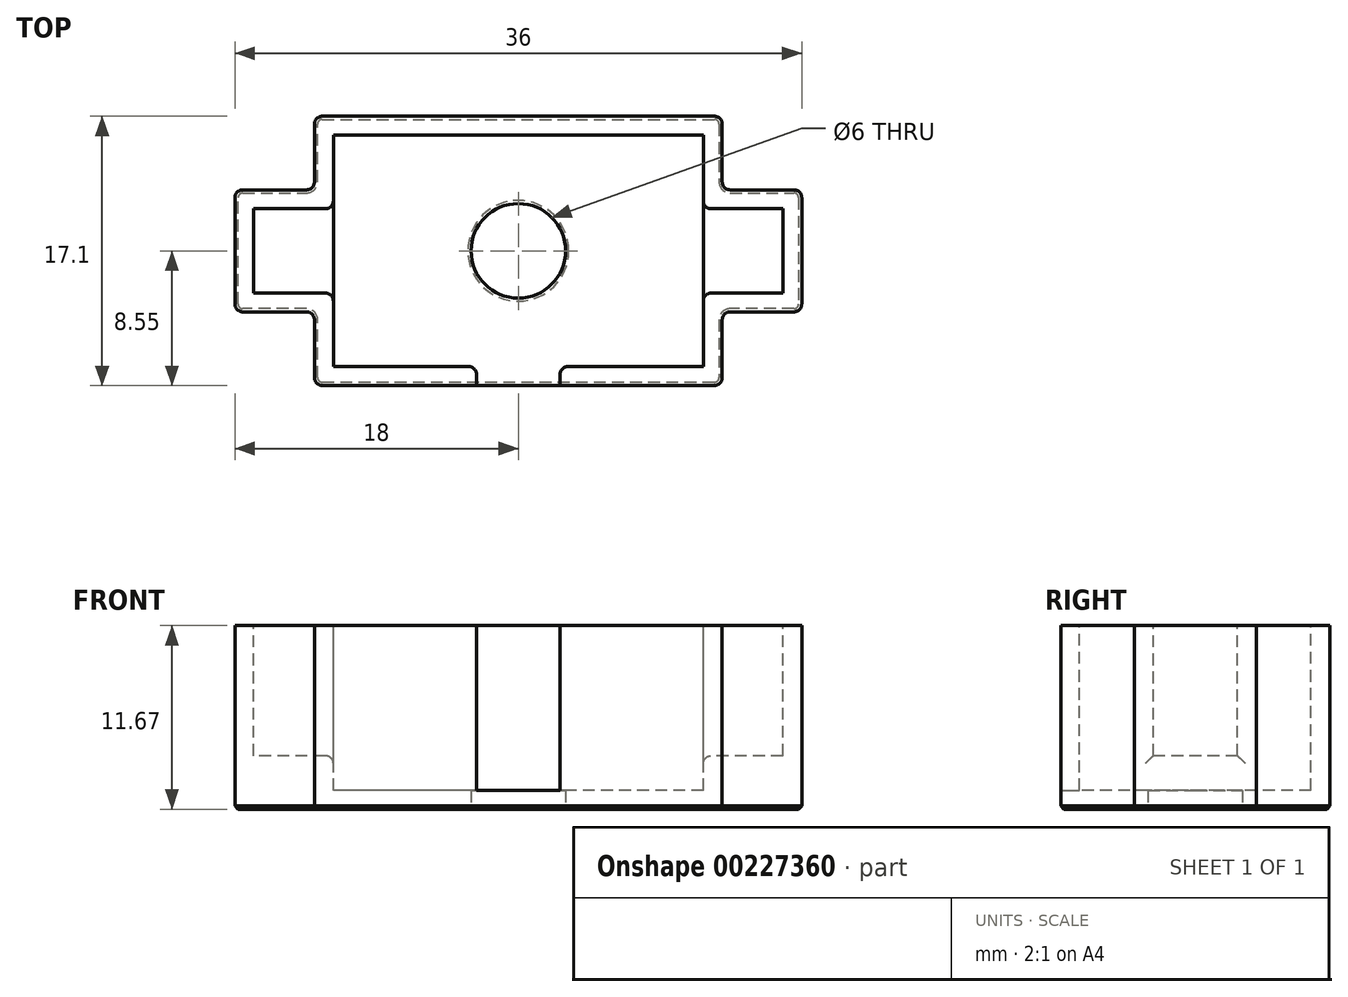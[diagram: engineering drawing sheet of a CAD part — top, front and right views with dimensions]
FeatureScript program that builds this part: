
annotation { "Feature Type Name" : "Feature", "Feature Type Description" : "" }
export const myFeature = defineFeature(function(context is Context, id is Id, definition is map)
    precondition{}
    {
        {
            var Q0;
            Q0=qCreatedBy(makeId("Top.planeOp"),FACE);
            var sketch = newSketch(context, id + "F0", { "sketchPlane" : qUnion([Q0])});
            skLineSegment(sketch, "E0.bottom", {"start": v(11.6, 7.2) * mm, "end": v(-11.6, 7.2) * mm, "construction": true});
            skLineSegment(sketch, "E0.top", {"start": v(11.6, -7.2) * mm, "end": v(2.5, -7.2) * mm, "construction": true});
            skLineSegment(sketch, "E0.left", {"start": v(11.6, 7.2) * mm, "end": v(11.6, 2.52) * mm, "construction": true});
            skLineSegment(sketch, "E0.right", {"start": v(-11.6, 7.2) * mm, "end": v(-11.6, 2.52) * mm, "construction": true});
            skPoint(sketch, "E0.middle", {"position": v(0, 0) * mm});
            skLineSegment(sketch, "E1.bottom", {"start": v(16.65, 2.52) * mm, "end": v(11.6, 2.52) * mm, "construction": true});
            skLineSegment(sketch, "E1.top", {"start": v(16.65, -2.52) * mm, "end": v(11.6, -2.52) * mm, "construction": true});
            skLineSegment(sketch, "E1.left", {"start": v(16.65, 2.52) * mm, "end": v(16.65, -2.52) * mm, "construction": true});
            skLineSegment(sketch, "E1.right", {"start": v(-16.65, 2.52) * mm, "end": v(-16.65, -2.52) * mm, "construction": true});
            skCircle(sketch, "E2", {"center": v(-14, 0) * mm, "radius": 1.5 * mm, "construction": true});
            skCircle(sketch, "E3.MirrorC", {"center": v(14, 0) * mm, "radius": 1.5 * mm, "construction": true});
            skLineSegment(sketch, "E4", {"start": v(-2.5, -7.2) * mm, "end": v(-2.5, -16.1) * mm, "construction": true});
            skLineSegment(sketch, "E5", {"start": v(-2.5, -16.1) * mm, "end": v(2.5, -16.1) * mm, "construction": true});
            skLineSegment(sketch, "E6", {"start": v(2.5, -16.1) * mm, "end": v(2.5, -7.2) * mm, "construction": true});
            skLineSegment(sketch, "E7", {"start": v(-2.5, -7.2) * mm, "end": v(-11.6, -7.2) * mm, "construction": true});
            skLineSegment(sketch, "E8", {"start": v(2.5, -7.2) * mm, "end": v(-2.5, -7.2) * mm, "construction": true});
            skLineSegment(sketch, "E9", {"start": v(-11.6, 2.52) * mm, "end": v(-16.65, 2.52) * mm, "construction": true});
            skLineSegment(sketch, "E10", {"start": v(-11.6, -2.52) * mm, "end": v(-16.65, -2.52) * mm, "construction": true});
            skLineSegment(sketch, "E11", {"start": v(11.6, -2.52) * mm, "end": v(-11.6, -2.52) * mm, "construction": true});
            skLineSegment(sketch, "E12", {"start": v(11.6, 2.52) * mm, "end": v(-11.6, 2.52) * mm, "construction": true});
            skLineSegment(sketch, "E13", {"start": v(-11.6, 2.52) * mm, "end": v(-11.6, -2.52) * mm, "construction": true});
            skLineSegment(sketch, "E14", {"start": v(-11.6, -2.52) * mm, "end": v(-11.6, -7.2) * mm, "construction": true});
            skLineSegment(sketch, "E15", {"start": v(11.6, -2.52) * mm, "end": v(11.6, -7.2) * mm, "construction": true});
            skLineSegment(sketch, "E16", {"start": v(11.6, 2.52) * mm, "end": v(11.6, -2.52) * mm, "construction": true});
            skSolve(sketch);
        }
        {
            var Q0;
            Q0=qCreatedBy(makeId("Front.planeOp"),FACE);
            var sketch = newSketch(context, id + "F1", { "sketchPlane" : qUnion([Q0])});
            skLineSegment(sketch, "E17", {"start": v(0, 1.2) * mm, "end": v(0, 0) * mm});
            skLineSegment(sketch, "E18", {"start": v(0, 1.2) * mm, "end": v(0, 3.4) * mm});
            skLineSegment(sketch, "E19", {"start": v(0, 3.4) * mm, "end": v(0, 4.67) * mm});
            skLineSegment(sketch, "E20", {"start": v(0, 4.67) * mm, "end": v(0, 11.67) * mm});
            skSolve(sketch);
        }
        {
            var Q0;
            Q0=sQuery(id+"F1.wireOp",VERTEX,"E17.start");
            var Q1;
            Q1=sQuery(id+"F1.wireOp",EDGE,"E18");
            cPlane(context, id + "F2", {"entities" : qUnion([Q0, Q1]), "cplaneType" : CPlaneType.LINE_POINT, "offset" : 25 * mm, "width" : 150 * mm, "height" : 150 * mm});
        }
        {
            var Q0;
            Q0=qCreatedBy(makeId("Top.planeOp"),FACE);
            var sketch = newSketch(context, id + "F3", { "sketchPlane" : qUnion([Q0])});
            skLineSegment(sketch, "E21.0", {"start": v(-16.65, 2.52) * mm, "end": v(-16.65, -2.52) * mm, "construction": true});
            skLineSegment(sketch, "E22.0", {"start": v(16.65, 2.52) * mm, "end": v(16.65, -2.52) * mm, "construction": true});
            skLineSegment(sketch, "E23.bottom", {"start": v(17.85, 8.4) * mm, "end": v(-17.85, 8.4) * mm});
            skLineSegment(sketch, "E23.top", {"start": v(17.85, -8.4) * mm, "end": v(-17.85, -8.4) * mm});
            skLineSegment(sketch, "E23.left", {"start": v(17.85, 8.4) * mm, "end": v(17.85, -8.4) * mm});
            skLineSegment(sketch, "E23.right", {"start": v(-17.85, 8.4) * mm, "end": v(-17.85, -8.4) * mm});
            skPoint(sketch, "E23.middle", {"position": v(0, 0) * mm});
            skLineSegment(sketch, "E24.0", {"start": v(11.6, 7.2) * mm, "end": v(-11.6, 7.2) * mm, "construction": true});
            skLineSegment(sketch, "E25.0", {"start": v(-2.5, -7.2) * mm, "end": v(-11.6, -7.2) * mm, "construction": true});
            skLineSegment(sketch, "E26.0", {"start": v(11.6, -7.2) * mm, "end": v(2.5, -7.2) * mm, "construction": true});
            skSolve(sketch);
        }
        {
            var Q0;
            Q0=qCreatedBy(id+"F2.planeOp",FACE);
            var sketch = newSketch(context, id + "F4", { "sketchPlane" : qUnion([Q0])});
            skLineSegment(sketch, "E27.0", {"start": v(11.75, 7.35) * mm, "end": v(11.75, 2.67) * mm});
            skLineSegment(sketch, "E27.1", {"start": v(16.8, 2.67) * mm, "end": v(11.75, 2.67) * mm});
            skLineSegment(sketch, "E27.2", {"start": v(16.8, 2.68) * mm, "end": v(16.8, -2.68) * mm});
            skLineSegment(sketch, "E27.3", {"start": v(16.8, -2.67) * mm, "end": v(11.75, -2.67) * mm});
            skLineSegment(sketch, "E27.4", {"start": v(11.75, -2.67) * mm, "end": v(11.75, -7.35) * mm});
            skLineSegment(sketch, "E27.5", {"start": v(-11.75, -2.67) * mm, "end": v(-16.8, -2.67) * mm});
            skLineSegment(sketch, "E27.6", {"start": v(-16.8, 2.67) * mm, "end": v(-16.8, -2.68) * mm});
            skLineSegment(sketch, "E27.7", {"start": v(-11.75, 2.67) * mm, "end": v(-16.8, 2.67) * mm});
            skLineSegment(sketch, "E27.8", {"start": v(-11.75, 7.35) * mm, "end": v(-11.75, 2.67) * mm});
            skLineSegment(sketch, "E27.9", {"start": v(-11.75, -2.68) * mm, "end": v(-11.75, -7.35) * mm});
            skLineSegment(sketch, "E27.10", {"start": v(-2.65, -7.35) * mm, "end": v(-11.75, -7.35) * mm});
            skLineSegment(sketch, "E27.11", {"start": v(-2.65, -7.35) * mm, "end": v(-2.65, -16.26) * mm});
            skLineSegment(sketch, "E27.12", {"start": v(-2.65, -16.26) * mm, "end": v(2.65, -16.26) * mm});
            skLineSegment(sketch, "E27.13", {"start": v(2.65, -16.26) * mm, "end": v(2.65, -7.35) * mm});
            skLineSegment(sketch, "E27.14", {"start": v(11.75, 7.35) * mm, "end": v(-11.75, 7.35) * mm});
            skLineSegment(sketch, "E27.15", {"start": v(11.75, -7.35) * mm, "end": v(2.65, -7.35) * mm});
            skLineSegment(sketch, "E28", {"start": v(-11.75, 2.67) * mm, "end": v(-11.75, -2.67) * mm});
            skLineSegment(sketch, "E29", {"start": v(11.75, 2.67) * mm, "end": v(11.75, -2.67) * mm});
            skSolve(sketch);
        }
        {
            var Q0;
            Q0=qCreatedBy(makeId("Top.planeOp"),FACE);
            var sketch = newSketch(context, id + "F5", { "sketchPlane" : qUnion([Q0])});
            skLineSegment(sketch, "E30.0", {"start": v(0, -8.55) * mm, "end": v(-12.95, -8.55) * mm});
            skLineSegment(sketch, "E30.1", {"start": v(-12.95, -3.87) * mm, "end": v(-12.95, -8.55) * mm});
            skLineSegment(sketch, "E30.2", {"start": v(-12.95, -3.87) * mm, "end": v(-18, -3.87) * mm});
            skLineSegment(sketch, "E30.3", {"start": v(18, 3.87) * mm, "end": v(18, -3.88) * mm});
            skLineSegment(sketch, "E30.4", {"start": v(18, -3.87) * mm, "end": v(12.95, -3.87) * mm});
            skLineSegment(sketch, "E30.5", {"start": v(12.95, -3.87) * mm, "end": v(12.95, -8.55) * mm});
            skLineSegment(sketch, "E30.6", {"start": v(12.95, -8.55) * mm, "end": v(0, -8.55) * mm});
            skLineSegment(sketch, "E30.7", {"start": v(18, 3.87) * mm, "end": v(12.95, 3.87) * mm});
            skLineSegment(sketch, "E30.8", {"start": v(12.95, 8.55) * mm, "end": v(12.95, 3.87) * mm});
            skLineSegment(sketch, "E30.9", {"start": v(12.95, 8.55) * mm, "end": v(-12.95, 8.55) * mm});
            skLineSegment(sketch, "E30.10", {"start": v(-12.95, 8.55) * mm, "end": v(-12.95, 3.87) * mm});
            skLineSegment(sketch, "E30.11", {"start": v(-12.95, 3.87) * mm, "end": v(-18, 3.87) * mm});
            skLineSegment(sketch, "E30.12", {"start": v(-18, 3.87) * mm, "end": v(-18, -3.87) * mm});
            skSolve(sketch);
        }
        {
            var Q0;
            Q0 = qSketchRegion(id + "F5", true);
            var Q1;
            Q1=sQuery(id+"F1.wireOp",EDGE,"E17");
            var Q2;
            Q2=sQuery(id+"F1.wireOp",EDGE,"E18");
            var Q3;
            Q3=sQuery(id+"F1.wireOp",EDGE,"E19");
            var Q4;
            Q4=sQuery(id+"F1.wireOp",EDGE,"E20");
            sweep(context, id + "F6", {"profiles" : qUnion([Q0]), "path" : qUnion([Q1, Q2, Q3, Q4])});
        }
        {
            var Q0;
            Q0 = qSketchRegion(id + "F4", true);
            var Q1;
            Q1=sQuery(id+"F1.wireOp",EDGE,"E18");
            var Q2;
            Q2=sQuery(id+"F1.wireOp",EDGE,"E19");
            var Q3;
            Q3=sQuery(id+"F1.wireOp",EDGE,"E20");
            sweep(context, id + "F7", {"operationType" : NewBodyOperationType.REMOVE, "profiles" : qUnion([Q0]), "path" : qUnion([Q1, Q2, Q3])});
        }
        {
            var Q0;
            Q0=makeQuery(id+"F4.imprint","IMPRINT",FACE,{"disambiguationData":[TD([[makeQuery(id+"F4.imprint","IMPRINT",EDGE,{"derivedFrom":sQuery(id+"F4.wireOp",EDGE,"E27.5")}),-1.0]])]});
            var Q1;
            Q1=makeQuery(id+"F4.imprint","IMPRINT",FACE,{"disambiguationData":[TD([[makeQuery(id+"F4.imprint","IMPRINT",EDGE,{"derivedFrom":sQuery(id+"F4.wireOp",EDGE,"E27.1")}),1.0]])]});
            var Q2;
            Q2=sQuery(id+"F1.wireOp",EDGE,"E18");
            sweep(context, id + "F8", {"operationType" : NewBodyOperationType.ADD, "profiles" : qUnion([Q0, Q1]), "path" : qUnion([Q2])});
        }
        {
            var Q0;
            Q0=qCreatedBy(makeId("Top.planeOp"),FACE);
            var sketch = newSketch(context, id + "F9", { "sketchPlane" : qUnion([Q0])});
            skCircle(sketch, "E31", {"center": v(0, 0) * mm, "radius": 3 * mm});
            skSolve(sketch);
        }
        {
            var Q0;
            Q0 = qSketchRegion(id + "F9", true);
            extrude(context, id + "F10", {"entities" : qUnion([Q0]), "operationType" : NewBodyOperationType.REMOVE, "endBound" : BoundingType.THROUGH_ALL, "depth" : 25 * mm});
        }
        {
            var Q0;
            Q0=makeQuery(id+"F7.boolean.opBoolean","COPY",EDGE,{"derivedFrom":makeQuery(id+"F7.opSweep","SWEPT_EDGE",EDGE,{"disambiguationData":[OSD([sQuery(id+"F1.wireOp",EDGE,"E18"),sQuery(id+"F4.wireOp",EDGE,"E27.7"),sQuery(id+"F4.wireOp",EDGE,"E27.8"),sQuery(id+"F4.wireOp",EDGE,"E28")])]})});
            var Q1;
            Q1=makeQuery(id+"F7.boolean.opBoolean","COPY",EDGE,{"derivedFrom":makeQuery(id+"F7.opSweep","SWEPT_EDGE",EDGE,{"disambiguationData":[OSD([sQuery(id+"F1.wireOp",EDGE,"E18"),sQuery(id+"F4.wireOp",EDGE,"E27.5"),sQuery(id+"F4.wireOp",EDGE,"E27.9"),sQuery(id+"F4.wireOp",EDGE,"E28")])]})});
            var Q2;
            Q2=makeQuery(id+"F7.boolean.opBoolean","COPY",EDGE,{"derivedFrom":makeQuery(id+"F7.opSweep","SWEPT_EDGE",EDGE,{"disambiguationData":[OSD([sQuery(id+"F1.wireOp",EDGE,"E18"),sQuery(id+"F4.wireOp",EDGE,"E27.0"),sQuery(id+"F4.wireOp",EDGE,"E27.1"),sQuery(id+"F4.wireOp",EDGE,"E29")])]})});
            var Q3;
            Q3=makeQuery(id+"F7.boolean.opBoolean","COPY",EDGE,{"derivedFrom":makeQuery(id+"F7.opSweep","SWEPT_EDGE",EDGE,{"disambiguationData":[OSD([sQuery(id+"F1.wireOp",EDGE,"E18"),sQuery(id+"F4.wireOp",EDGE,"E27.3"),sQuery(id+"F4.wireOp",EDGE,"E27.4"),sQuery(id+"F4.wireOp",EDGE,"E29")])]})});
            var Q4;
            Q4=makeQuery(id+"F7.boolean.opBoolean","COPY",EDGE,{"derivedFrom":makeQuery(id+"F7.opSweep","SWEPT_EDGE",EDGE,{"disambiguationData":[OSD([sQuery(id+"F1.wireOp",EDGE,"E18"),sQuery(id+"F4.wireOp",EDGE,"E27.10"),sQuery(id+"F4.wireOp",EDGE,"E27.11")])]})});
            var Q5;
            Q5=makeQuery(id+"F7.boolean.opBoolean","COPY",EDGE,{"derivedFrom":makeQuery(id+"F7.opSweep","SWEPT_EDGE",EDGE,{"disambiguationData":[OSD([sQuery(id+"F1.wireOp",EDGE,"E18"),sQuery(id+"F4.wireOp",EDGE,"E27.13"),sQuery(id+"F4.wireOp",EDGE,"E27.15")])]})});
            var Q6;
            Q6=makeQuery(id+"F8.opSweep","CAP_EDGE",EDGE,{"disambiguationData":[OSD([sQuery(id+"F1.wireOp",VERTEX,"E18.end"),sQuery(id+"F4.wireOp",EDGE,"E28")])],"isStart":false});
            var Q7;
            Q7=makeQuery(id+"F8.opSweep","CAP_EDGE",EDGE,{"disambiguationData":[OSD([sQuery(id+"F1.wireOp",VERTEX,"E18.end"),sQuery(id+"F4.wireOp",EDGE,"E29")])],"isStart":false});
            var Q8;
            Q8=makeQuery(id+"F6.opSweep","SWEPT_EDGE",EDGE,{"disambiguationData":[OSD([sQuery(id+"F1.wireOp",EDGE,"E17"),sQuery(id+"F5.wireOp",EDGE,"E30.3"),sQuery(id+"F5.wireOp",EDGE,"E30.4")])]});
            var Q9;
            Q9=makeQuery(id+"F6.opSweep","SWEPT_EDGE",EDGE,{"disambiguationData":[OSD([sQuery(id+"F1.wireOp",EDGE,"E17"),sQuery(id+"F5.wireOp",EDGE,"E30.3"),sQuery(id+"F5.wireOp",EDGE,"E30.7")])]});
            var Q10;
            Q10=makeQuery(id+"F6.opSweep","SWEPT_EDGE",EDGE,{"disambiguationData":[OSD([sQuery(id+"F1.wireOp",EDGE,"E17"),sQuery(id+"F5.wireOp",EDGE,"E30.5"),sQuery(id+"F5.wireOp",EDGE,"E30.6")])]});
            var Q11;
            Q11=makeQuery(id+"F6.opSweep","SWEPT_EDGE",EDGE,{"disambiguationData":[OSD([sQuery(id+"F1.wireOp",EDGE,"E17"),sQuery(id+"F5.wireOp",EDGE,"E30.8"),sQuery(id+"F5.wireOp",EDGE,"E30.9")])]});
            var Q12;
            Q12=makeQuery(id+"F6.opSweep","SWEPT_EDGE",EDGE,{"disambiguationData":[OSD([sQuery(id+"F1.wireOp",EDGE,"E17"),sQuery(id+"F5.wireOp",EDGE,"E30.0"),sQuery(id+"F5.wireOp",EDGE,"E30.1")])]});
            var Q13;
            Q13=makeQuery(id+"F6.opSweep","SWEPT_EDGE",EDGE,{"disambiguationData":[OSD([sQuery(id+"F1.wireOp",EDGE,"E17"),sQuery(id+"F5.wireOp",EDGE,"E30.2"),sQuery(id+"F5.wireOp",EDGE,"E30.12")])]});
            var Q14;
            Q14=makeQuery(id+"F6.opSweep","SWEPT_EDGE",EDGE,{"disambiguationData":[OSD([sQuery(id+"F1.wireOp",EDGE,"E17"),sQuery(id+"F5.wireOp",EDGE,"E30.9"),sQuery(id+"F5.wireOp",EDGE,"E30.10")])]});
            var Q15;
            Q15=makeQuery(id+"F6.opSweep","SWEPT_EDGE",EDGE,{"disambiguationData":[OSD([sQuery(id+"F1.wireOp",EDGE,"E17"),sQuery(id+"F5.wireOp",EDGE,"E30.11"),sQuery(id+"F5.wireOp",EDGE,"E30.12")])]});
            var Q16;
            Q16=makeQuery(id+"F6.opSweep","SWEPT_EDGE",EDGE,{"disambiguationData":[OSD([sQuery(id+"F1.wireOp",EDGE,"E17"),sQuery(id+"F5.wireOp",EDGE,"E30.7"),sQuery(id+"F5.wireOp",EDGE,"E30.8")])]});
            var Q17;
            Q17=makeQuery(id+"F6.opSweep","SWEPT_EDGE",EDGE,{"disambiguationData":[OSD([sQuery(id+"F1.wireOp",EDGE,"E17"),sQuery(id+"F5.wireOp",EDGE,"E30.4"),sQuery(id+"F5.wireOp",EDGE,"E30.5")])]});
            var Q18;
            Q18=makeQuery(id+"F6.opSweep","SWEPT_EDGE",EDGE,{"disambiguationData":[OSD([sQuery(id+"F1.wireOp",EDGE,"E17"),sQuery(id+"F5.wireOp",EDGE,"E30.1"),sQuery(id+"F5.wireOp",EDGE,"E30.2")])]});
            var Q19;
            Q19=makeQuery(id+"F6.opSweep","SWEPT_EDGE",EDGE,{"disambiguationData":[OSD([sQuery(id+"F1.wireOp",EDGE,"E17"),sQuery(id+"F5.wireOp",EDGE,"E30.10"),sQuery(id+"F5.wireOp",EDGE,"E30.11")])]});
            fillet(context, id + "F11", {"entities" : qUnion([Q0, Q1, Q2, Q3, Q4, Q5, Q6, Q7, Q8, Q9, Q10, Q11, Q12, Q13, Q14, Q15, Q16, Q17, Q18, Q19]), "radius" : 0.5 * mm, "allowEdgeOverflow" : false});
        }
        {
            var Q0;
            Q0=makeQuery(id+"F6.opSweep","CAP_FACE",FACE,{"disambiguationData":[OSD([sQuery(id+"F1.wireOp",VERTEX,"E17.end"),sQuery(id+"F3.wireOp",EDGE,"E23.bottom"),sQuery(id+"F3.wireOp",EDGE,"E23.top"),sQuery(id+"F3.wireOp",EDGE,"E23.left"),sQuery(id+"F3.wireOp",EDGE,"E23.right")])],"isStart":true});
            chamfer(context, id + "F12", {"entities" : qUnion([Q0]), "width" : 0.2 * mm});
        }
    });
